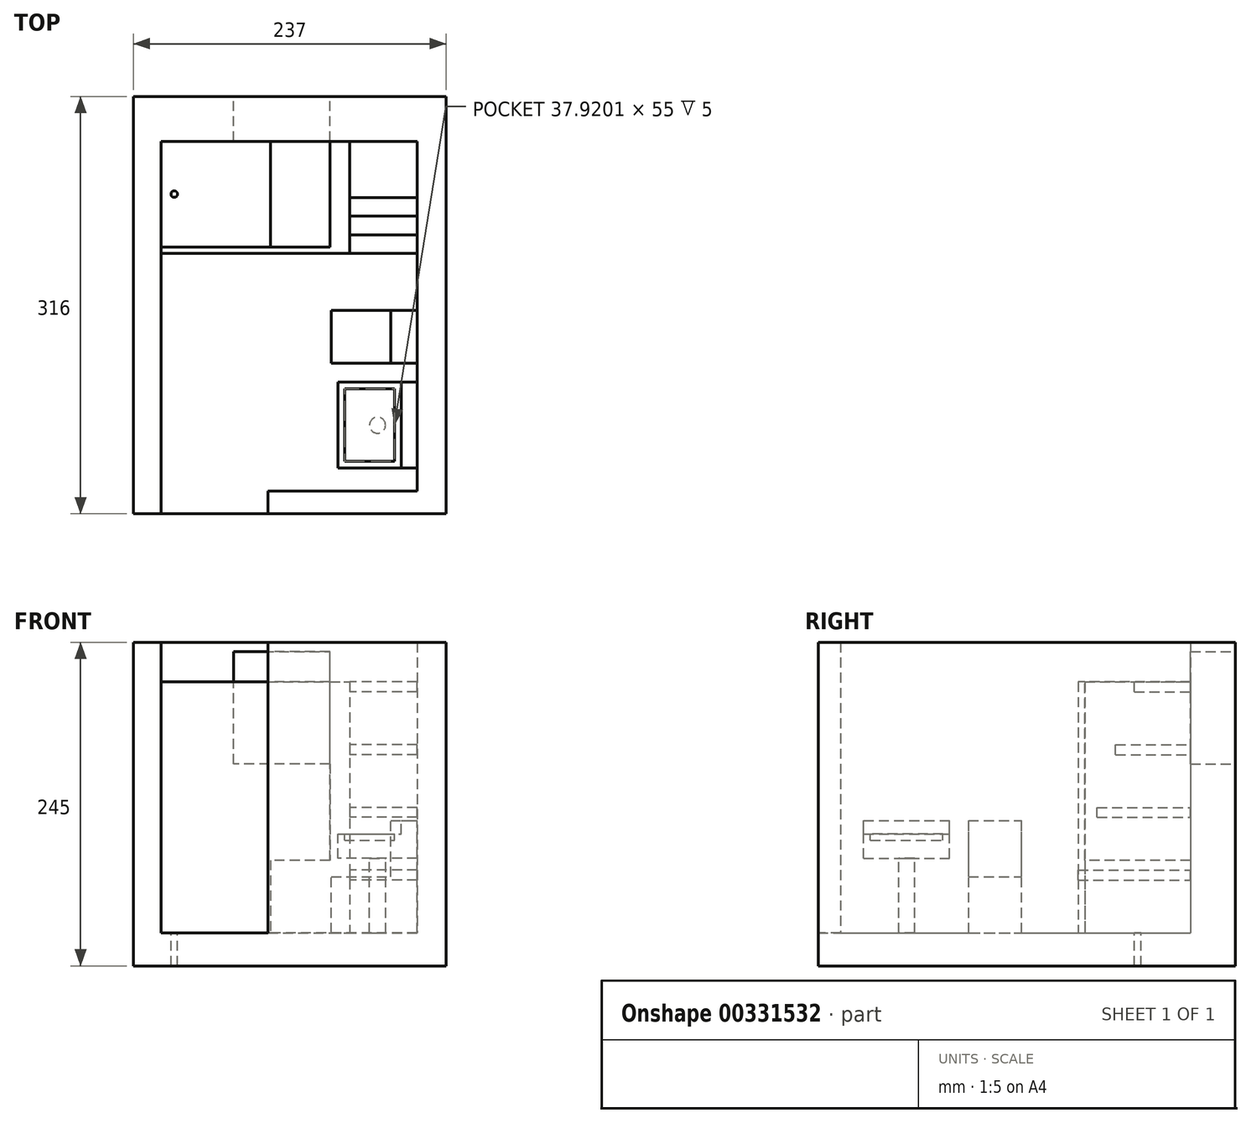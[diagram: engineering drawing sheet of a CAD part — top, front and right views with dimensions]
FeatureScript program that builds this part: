
annotation { "Feature Type Name" : "Feature", "Feature Type Description" : "" }
export const myFeature = defineFeature(function(context is Context, id is Id, definition is map)
    precondition{}
    {
        {
            var Q0;
            Q0=qCreatedBy(makeId("Top.planeOp"),FACE);
            var sketch = newSketch(context, id + "F0", { "sketchPlane" : qUnion([Q0])});
            skLineSegment(sketch, "E0", {"start": v(1313, 440) * mm, "end": v(1313, 406) * mm});
            skLineSegment(sketch, "E1", {"start": v(1313, -267) * mm, "end": v(1313, -301) * mm});
            skLineSegment(sketch, "E2", {"start": v(1313, -301) * mm, "end": v(647, -301) * mm});
            skLineSegment(sketch, "E3", {"start": v(1279, -267) * mm, "end": v(647, -267) * mm});
            skLineSegment(sketch, "E4", {"start": v(1279, 406) * mm, "end": v(688, 406) * mm});
            skLineSegment(sketch, "E5", {"start": v(688, 406) * mm, "end": v(688, -75) * mm});
            skLineSegment(sketch, "E6", {"start": v(688, -75) * mm, "end": v(413, -75) * mm});
            skLineSegment(sketch, "E7", {"start": v(647, -301) * mm, "end": v(647, -267) * mm});
            skLineSegment(sketch, "E8", {"start": v(536, -301) * mm, "end": v(536, -267) * mm});
            skLineSegment(sketch, "E9", {"start": v(536, -267) * mm, "end": v(328, -267) * mm});
            skLineSegment(sketch, "E10", {"start": v(328, -267) * mm, "end": v(328, -407) * mm});
            skLineSegment(sketch, "E11", {"start": v(328, -407) * mm, "end": v(-40, -407) * mm});
            skLineSegment(sketch, "E12", {"start": v(-40, -407) * mm, "end": v(-40, -188) * mm});
            skLineSegment(sketch, "E13", {"start": v(-40, -188) * mm, "end": v(-105, -188) * mm});
            skLineSegment(sketch, "E14", {"start": v(536, -301) * mm, "end": v(362, -301) * mm});
            skLineSegment(sketch, "E15", {"start": v(362, -301) * mm, "end": v(362, -440) * mm});
            skLineSegment(sketch, "E16", {"start": v(-60, -407) * mm, "end": v(-60, -215) * mm});
            skLineSegment(sketch, "E17", {"start": v(-60, -215) * mm, "end": v(-105, -215) * mm});
            skLineSegment(sketch, "E18", {"start": v(-105, -188) * mm, "end": v(-105, -215) * mm});
            skLineSegment(sketch, "E19", {"start": v(-60, -407) * mm, "end": v(-282, -407) * mm});
            skLineSegment(sketch, "E20", {"start": v(-282, -407) * mm, "end": v(-282, -287) * mm});
            skLineSegment(sketch, "E21", {"start": v(-282, -287) * mm, "end": v(-330, -287) * mm});
            skLineSegment(sketch, "E22", {"start": v(-330, -287) * mm, "end": v(-330, -407) * mm});
            skLineSegment(sketch, "E23", {"start": v(-330, -407) * mm, "end": v(-497, -407) * mm});
            skLineSegment(sketch, "E24", {"start": v(-197, -188) * mm, "end": v(-197, -215) * mm});
            skLineSegment(sketch, "E25", {"start": v(-197, -188) * mm, "end": v(-765, -188) * mm});
            skLineSegment(sketch, "E26", {"start": v(-197, -215) * mm, "end": v(-497, -215) * mm});
            skLineSegment(sketch, "E27", {"start": v(-497, -215) * mm, "end": v(-497, -231) * mm});
            skLineSegment(sketch, "E28", {"start": v(-497, -231) * mm, "end": v(-497, -293) * mm});
            skLineSegment(sketch, "E29", {"start": v(-497, -407) * mm, "end": v(-497, -349) * mm});
            skLineSegment(sketch, "E30", {"start": v(413, -75) * mm, "end": v(413, -54) * mm});
            skLineSegment(sketch, "E31", {"start": v(413, -54) * mm, "end": v(667, -54) * mm});
            skLineSegment(sketch, "E32", {"start": v(667, -54) * mm, "end": v(667, 406) * mm});
            skLineSegment(sketch, "E33", {"start": v(667, 406) * mm, "end": v(495, 406) * mm});
            skLineSegment(sketch, "E34", {"start": v(312, 406) * mm, "end": v(391, 406) * mm});
            skLineSegment(sketch, "E35", {"start": v(391, 406) * mm, "end": v(391, 440) * mm});
            skLineSegment(sketch, "E36", {"start": v(495, 406) * mm, "end": v(495, 440) * mm});
            skLineSegment(sketch, "E37", {"start": v(1313, 440) * mm, "end": v(495, 440) * mm});
            skLineSegment(sketch, "E38", {"start": v(312, -75) * mm, "end": v(60, -75) * mm});
            skLineSegment(sketch, "E39", {"start": v(-1279, 406) * mm, "end": v(-1279, 7) * mm});
            skLineSegment(sketch, "E40", {"start": v(-790, 406) * mm, "end": v(-790, 7) * mm});
            skLineSegment(sketch, "E41", {"start": v(-1279, 7) * mm, "end": v(-910, 7) * mm});
            skLineSegment(sketch, "E42", {"start": v(-790, 7) * mm, "end": v(-808, 7) * mm});
            skLineSegment(sketch, "E43", {"start": v(-765, -188) * mm, "end": v(-765, -208) * mm});
            skLineSegment(sketch, "E44", {"start": v(290, 141) * mm, "end": v(290, 406) * mm});
            skLineSegment(sketch, "E45", {"start": v(290, 141) * mm, "end": v(75, 141) * mm});
            skLineSegment(sketch, "E46", {"start": v(75, -46) * mm, "end": v(75, 141) * mm});
            skLineSegment(sketch, "E47", {"start": v(60, -75) * mm, "end": v(60, -46) * mm});
            skLineSegment(sketch, "E48", {"start": v(391, 406) * mm, "end": v(312, 406) * mm});
            skLineSegment(sketch, "E49", {"start": v(-139, 406) * mm, "end": v(-139, 440) * mm});
            skLineSegment(sketch, "E50", {"start": v(-318, 406) * mm, "end": v(-318, 440) * mm});
            skLineSegment(sketch, "E51", {"start": v(-515, 406) * mm, "end": v(-515, 440) * mm});
            skLineSegment(sketch, "E52", {"start": v(-694, 406) * mm, "end": v(-694, 440) * mm});
            skLineSegment(sketch, "E53", {"start": v(-770, 406) * mm, "end": v(-770, 9) * mm});
            skLineSegment(sketch, "E54", {"start": v(-694, 406) * mm, "end": v(-770, 406) * mm});
            skLineSegment(sketch, "E55", {"start": v(75, 406) * mm, "end": v(-139, 406) * mm});
            skLineSegment(sketch, "E56", {"start": v(-318, 406) * mm, "end": v(-515, 406) * mm});
            skLineSegment(sketch, "E57", {"start": v(-318, 440) * mm, "end": v(-515, 440) * mm});
            skLineSegment(sketch, "E58", {"start": v(-770, 9) * mm, "end": v(-754, 9) * mm});
            skLineSegment(sketch, "E59", {"start": v(-677, 9) * mm, "end": v(-659, 9) * mm});
            skLineSegment(sketch, "E60", {"start": v(-659, 9) * mm, "end": v(-659, -5) * mm});
            skLineSegment(sketch, "E61", {"start": v(-659, -5) * mm, "end": v(-659, -46) * mm});
            skLineSegment(sketch, "E62", {"start": v(-659, -46) * mm, "end": v(-60, -46) * mm});
            skLineSegment(sketch, "E63", {"start": v(-60, -75) * mm, "end": v(-60, -46) * mm});
            skLineSegment(sketch, "E64", {"start": v(60, -75) * mm, "end": v(128, -75) * mm});
            skLineSegment(sketch, "E65", {"start": v(60, -46) * mm, "end": v(75, -46) * mm});
            skLineSegment(sketch, "E66", {"start": v(96, -46) * mm, "end": v(290, -46) * mm});
            skLineSegment(sketch, "E67", {"start": v(-60, -75) * mm, "end": v(-677, -75) * mm});
            skLineSegment(sketch, "E68", {"start": v(-677, 9) * mm, "end": v(-677, -75) * mm});
            skLineSegment(sketch, "E69", {"start": v(-754, 9) * mm, "end": v(-754, -13) * mm});
            skLineSegment(sketch, "E70", {"start": v(-808, 7) * mm, "end": v(-808, -13) * mm});
            skLineSegment(sketch, "E71", {"start": v(-808, -13) * mm, "end": v(-754, -13) * mm});
            skLineSegment(sketch, "E72", {"start": v(-910, 7) * mm, "end": v(-910, -29) * mm});
            skLineSegment(sketch, "E73", {"start": v(-1279, -406) * mm, "end": v(-935, -406) * mm});
            skLineSegment(sketch, "E74", {"start": v(-1313, -440) * mm, "end": v(-935, -440) * mm});
            skLineSegment(sketch, "E75", {"start": v(-910, -29) * mm, "end": v(-935, -29) * mm});
            skLineSegment(sketch, "E76", {"start": v(-935, -13) * mm, "end": v(-1279, -13) * mm});
            skLineSegment(sketch, "E77", {"start": v(-910, -132) * mm, "end": v(-935, -132) * mm});
            skLineSegment(sketch, "E78", {"start": v(-910, -29) * mm, "end": v(-910, -13) * mm});
            skLineSegment(sketch, "E79", {"start": v(-935, -406) * mm, "end": v(-935, -132) * mm});
            skLineSegment(sketch, "E80", {"start": v(-935, -29) * mm, "end": v(-935, -13) * mm});
            skLineSegment(sketch, "E81", {"start": v(-877, -208) * mm, "end": v(-877, -188) * mm});
            skLineSegment(sketch, "E82", {"start": v(-910, -132) * mm, "end": v(-910, -188) * mm});
            skLineSegment(sketch, "E83", {"start": v(-877, -188) * mm, "end": v(-910, -188) * mm});
            skLineSegment(sketch, "E84", {"start": v(-877, -208) * mm, "end": v(-904, -208) * mm});
            skLineSegment(sketch, "E85", {"start": v(-904, -208) * mm, "end": v(-904, -406) * mm});
            skLineSegment(sketch, "E86", {"start": v(-904, -406) * mm, "end": v(-648, -406) * mm});
            skLineSegment(sketch, "E87", {"start": v(-765, -208) * mm, "end": v(-648, -208) * mm});
            skLineSegment(sketch, "E88", {"start": v(-648, -208) * mm, "end": v(-648, -273) * mm});
            skLineSegment(sketch, "E89", {"start": v(-648, -406) * mm, "end": v(-648, -343) * mm});
            skLineSegment(sketch, "E90", {"start": v(-935, -440) * mm, "end": v(362, -440) * mm});
            skLineSegment(sketch, "E91", {"start": v(151, 406) * mm, "end": v(151, 440) * mm});
            skLineSegment(sketch, "E92", {"start": v(224, 406) * mm, "end": v(224, 440) * mm});
            skLineSegment(sketch, "E93", {"start": v(290, 406) * mm, "end": v(224, 406) * mm});
            skLineSegment(sketch, "E94", {"start": v(151, 406) * mm, "end": v(96, 406) * mm});
            skLineSegment(sketch, "E95", {"start": v(391, 440) * mm, "end": v(224, 440) * mm});
            skLineSegment(sketch, "E96", {"start": v(151, 440) * mm, "end": v(-139, 440) * mm});
            skLineSegment(sketch, "E97", {"start": v(-907, 406) * mm, "end": v(-907, 440) * mm});
            skLineSegment(sketch, "E98", {"start": v(-1085, 406) * mm, "end": v(-1085, 440) * mm});
            skLineSegment(sketch, "E99", {"start": v(-790, 406) * mm, "end": v(-907, 406) * mm});
            skLineSegment(sketch, "E100", {"start": v(-1085, 406) * mm, "end": v(-1279, 406) * mm});
            skLineSegment(sketch, "E101", {"start": v(-694, 440) * mm, "end": v(-907, 440) * mm});
            skLineSegment(sketch, "E102", {"start": v(-1085, 440) * mm, "end": v(-1313, 440) * mm});
            skLineSegment(sketch, "E103", {"start": v(-1279, -118) * mm, "end": v(-1313, -118) * mm});
            skLineSegment(sketch, "E104", {"start": v(-1279, -297) * mm, "end": v(-1313, -297) * mm});
            skLineSegment(sketch, "E105", {"start": v(-1279, -13) * mm, "end": v(-1279, -118) * mm});
            skLineSegment(sketch, "E106", {"start": v(-1279, -297) * mm, "end": v(-1279, -406) * mm});
            skLineSegment(sketch, "E107", {"start": v(-1313, 440) * mm, "end": v(-1313, -118) * mm});
            skLineSegment(sketch, "E108", {"start": v(-1313, -297) * mm, "end": v(-1313, -440) * mm});
            skLineSegment(sketch, "E109", {"start": v(-648, -273) * mm, "end": v(-630, -273) * mm});
            skLineSegment(sketch, "E110", {"start": v(-648, -343) * mm, "end": v(-630, -343) * mm});
            skLineSegment(sketch, "E111", {"start": v(-515, -349) * mm, "end": v(-497, -349) * mm});
            skLineSegment(sketch, "E112", {"start": v(-515, -293) * mm, "end": v(-497, -293) * mm});
            skLineSegment(sketch, "E113", {"start": v(-515, -349) * mm, "end": v(-515, -406) * mm});
            skLineSegment(sketch, "E114", {"start": v(-630, -343) * mm, "end": v(-630, -406) * mm});
            skLineSegment(sketch, "E115", {"start": v(-630, -406) * mm, "end": v(-515, -406) * mm});
            skLineSegment(sketch, "E116", {"start": v(-630, -273) * mm, "end": v(-630, -206) * mm});
            skLineSegment(sketch, "E117", {"start": v(-630, -206) * mm, "end": v(-515, -206) * mm});
            skLineSegment(sketch, "E118", {"start": v(-515, -293) * mm, "end": v(-515, -206) * mm});
            skLineSegment(sketch, "E119", {"start": v(290, 43) * mm, "end": v(312, 43) * mm});
            skLineSegment(sketch, "E120", {"start": v(290, 124) * mm, "end": v(312, 124) * mm});
            skLineSegment(sketch, "E121", {"start": v(312, -75) * mm, "end": v(312, 43) * mm});
            skLineSegment(sketch, "E122", {"start": v(312, 124) * mm, "end": v(312, 406) * mm});
            skLineSegment(sketch, "E123", {"start": v(290, -46) * mm, "end": v(290, 43) * mm});
            skLineSegment(sketch, "E124", {"start": v(96, 222) * mm, "end": v(75, 222) * mm});
            skLineSegment(sketch, "E125", {"start": v(96, 222) * mm, "end": v(96, 406) * mm});
            skLineSegment(sketch, "E126", {"start": v(75, 222) * mm, "end": v(75, 406) * mm});
            skLineSegment(sketch, "E127", {"start": v(96, -46) * mm, "end": v(96, 124) * mm});
            skLineSegment(sketch, "E128", {"start": v(290, 124) * mm, "end": v(96, 124) * mm});
            skLineSegment(sketch, "E129", {"start": v(1279, -219) * mm, "end": v(1313, -219) * mm});
            skLineSegment(sketch, "E130", {"start": v(1279, -26) * mm, "end": v(1313, -26) * mm});
            skLineSegment(sketch, "E131", {"start": v(1279, 46) * mm, "end": v(1313, 46) * mm});
            skLineSegment(sketch, "E132", {"start": v(1279, 239) * mm, "end": v(1313, 239) * mm});
            skLineSegment(sketch, "E133", {"start": v(1313, 406) * mm, "end": v(1313, 239) * mm});
            skLineSegment(sketch, "E134", {"start": v(1279, 406) * mm, "end": v(1279, 239) * mm});
            skLineSegment(sketch, "E135", {"start": v(1313, 46) * mm, "end": v(1313, -26) * mm});
            skLineSegment(sketch, "E136", {"start": v(1313, -219) * mm, "end": v(1313, -267) * mm});
            skLineSegment(sketch, "E137", {"start": v(1279, 46) * mm, "end": v(1279, -26) * mm});
            skLineSegment(sketch, "E138", {"start": v(1279, -219) * mm, "end": v(1279, -267) * mm});
            skLineSegment(sketch, "E139", {"start": v(1313, -301) * mm, "end": v(1313, 440) * mm});
            skLineSegment(sketch, "E140", {"start": v(1313, -301) * mm, "end": v(362, -301) * mm});
            skLineSegment(sketch, "E141", {"start": v(362, -440) * mm, "end": v(-1313, -440) * mm});
            skLineSegment(sketch, "E142", {"start": v(-1313, 440) * mm, "end": v(-1313, -440) * mm});
            skLineSegment(sketch, "E143", {"start": v(-1313, 440) * mm, "end": v(1313, 440) * mm});
            skSolve(sketch);
        }
        {
            var Q0;
            Q0=qCreatedBy(makeId("Top.planeOp"),FACE);
            var sketch = newSketch(context, id + "F1", { "sketchPlane" : qUnion([Q0])});
            skLineSegment(sketch, "E144.0", {"start": v(290, 406) * mm, "end": v(224, 406) * mm});
            skLineSegment(sketch, "E145.0", {"start": v(75, 440) * mm, "end": v(312, 440) * mm});
            skLineSegment(sketch, "E146.0", {"start": v(151, 406) * mm, "end": v(96, 406) * mm});
            skLineSegment(sketch, "E147.0", {"start": v(96, 222) * mm, "end": v(96, 406) * mm});
            skLineSegment(sketch, "E148.0", {"start": v(312, 124) * mm, "end": v(312, 406) * mm});
            skLineSegment(sketch, "E149.0", {"start": v(290, 141) * mm, "end": v(290, 406) * mm});
            skLineSegment(sketch, "E150.0", {"start": v(75, 124) * mm, "end": v(75, 141) * mm});
            skLineSegment(sketch, "E151", {"start": v(312, 406) * mm, "end": v(312, 440) * mm});
            skLineSegment(sketch, "E152", {"start": v(75, 406) * mm, "end": v(75, 440) * mm});
            skLineSegment(sketch, "E153", {"start": v(151, 406) * mm, "end": v(224, 406) * mm});
            skLineSegment(sketch, "E154", {"start": v(290, 124) * mm, "end": v(312, 124) * mm});
            skLineSegment(sketch, "E155", {"start": v(96, 124) * mm, "end": v(75, 124) * mm});
            skPoint(sketch, "E156.orphan", {"position": v(1313, 440) * mm});
            skPoint(sketch, "E157.orphan", {"position": v(75, -46) * mm});
            skPoint(sketch, "E158.orphan", {"position": v(-1313, 440) * mm});
            skPoint(sketch, "E159.end.orphan", {"position": v(96, 141) * mm});
            skPoint(sketch, "E160.orphan", {"position": v(290, 141) * mm});
            skLineSegment(sketch, "E161", {"start": v(290, 141) * mm, "end": v(177, 141) * mm});
            skLineSegment(sketch, "E162", {"start": v(290, 124) * mm, "end": v(177, 124) * mm});
            skPoint(sketch, "E163.end.orphan", {"position": v(75, 141) * mm});
            skPoint(sketch, "E164.0.start.orphan", {"position": v(75, 222) * mm});
            skLineSegment(sketch, "E165", {"start": v(75, 406) * mm, "end": v(75, 141) * mm});
            skLineSegment(sketch, "E166", {"start": v(96, 124) * mm, "end": v(96, 222) * mm});
            skLineSegment(sketch, "E167", {"start": v(177, 141) * mm, "end": v(177, 124) * mm});
            skSolve(sketch);
        }
        {
            var Q0;
            Q0 = qSketchRegion(id + "F1", true);
            extrude(context, id + "F2", {"entities" : qUnion([Q0]), "depth" : 220 * mm});
        }
        {
            var Q0;
            Q0=makeQuery(id+"F2.opExtrude","CAP_FACE",FACE,{"disambiguationData":[OSD([sQuery(id+"F1.wireOp",EDGE,"E144.0"),sQuery(id+"F1.wireOp",EDGE,"E145.0"),sQuery(id+"F1.wireOp",EDGE,"E146.0"),sQuery(id+"F1.wireOp",EDGE,"E147.0"),sQuery(id+"F1.wireOp",EDGE,"E148.0"),sQuery(id+"F1.wireOp",EDGE,"E149.0"),sQuery(id+"F1.wireOp",EDGE,"E150.0"),sQuery(id+"F1.wireOp",EDGE,"E151"),sQuery(id+"F1.wireOp",EDGE,"E152"),sQuery(id+"F1.wireOp",EDGE,"E153"),sQuery(id+"F1.wireOp",EDGE,"E154"),sQuery(id+"F1.wireOp",EDGE,"E155"),sQuery(id+"F1.wireOp",EDGE,"E161"),sQuery(id+"F1.wireOp",EDGE,"E162"),sQuery(id+"F1.wireOp",EDGE,"E165"),sQuery(id+"F1.wireOp",EDGE,"E166"),sQuery(id+"F1.wireOp",EDGE,"E167")])],"isStart":false});
            var sketch = newSketch(context, id + "F3", { "sketchPlane" : qUnion([Q0])});
            skLineSegment(sketch, "E168", {"start": v(151, 406) * mm, "end": v(151, 440) * mm});
            skLineSegment(sketch, "E169", {"start": v(224, 406) * mm, "end": v(224, 440) * mm});
            skLineSegment(sketch, "E170.0", {"start": v(151, 406) * mm, "end": v(224, 406) * mm});
            skLineSegment(sketch, "E171", {"start": v(224, 440) * mm, "end": v(151, 440) * mm});
            skPoint(sketch, "E172.0.start.orphan", {"position": v(290, 406) * mm});
            skPoint(sketch, "E173.0.end.orphan", {"position": v(96, 406) * mm});
            skSolve(sketch);
        }
        {
            var Q0;
            Q0 = qSketchRegion(id + "F3", true);
            extrude(context, id + "F4", {"entities" : qUnion([Q0]), "operationType" : NewBodyOperationType.REMOVE, "oppositeDirection" : true, "depth" : 92 * mm});
        }
        {
            var Q0;
            {var subQ0=sQuery(id+"F1.wireOp",EDGE,"E166");var subQ1=sQuery(id+"F1.wireOp",EDGE,"E147.0");var subQ2=sQuery(id+"F1.wireOp",EDGE,"E145.0");var subQ3=sQuery(id+"F1.wireOp",EDGE,"E165");var subQ4=sQuery(id+"F1.wireOp",EDGE,"E152");var subQ5=sQuery(id+"F1.wireOp",EDGE,"E150.0");var subQ6=sQuery(id+"F1.wireOp",EDGE,"E153");var subQ7=sQuery(id+"F1.wireOp",EDGE,"E146.0");var subQ8=sQuery(id+"F1.wireOp",EDGE,"E144.0");var subQ9=sQuery(id+"F1.wireOp",EDGE,"E155");Q0=makeQuery(id+"F4.boolean.opBoolean","SPLIT",FACE,{"disambiguationData":[TD([makeQuery(id+"F2.opExtrude","SWEPT_FACE",FACE,{"disambiguationData":[OSD([subQ9])]})])],"derivedFrom":makeQuery(id+"F2.opExtrude","CAP_FACE",FACE,{"disambiguationData":[OSD([subQ8,subQ2,subQ7,subQ1,sQuery(id+"F1.wireOp",EDGE,"E148.0"),sQuery(id+"F1.wireOp",EDGE,"E149.0"),subQ5,sQuery(id+"F1.wireOp",EDGE,"E151"),subQ4,subQ6,sQuery(id+"F1.wireOp",EDGE,"E154"),subQ9,sQuery(id+"F1.wireOp",EDGE,"E161"),sQuery(id+"F1.wireOp",EDGE,"E162"),subQ3,subQ0,sQuery(id+"F1.wireOp",EDGE,"E167")])],"isStart":false})});}
            var sketch = newSketch(context, id + "F5", { "sketchPlane" : qUnion([Q0])});
            skLineSegment(sketch, "E174.0", {"start": v(151, 440) * mm, "end": v(224, 440) * mm});
            skLineSegment(sketch, "E175.0", {"start": v(224, 406) * mm, "end": v(151, 406) * mm});
            skPoint(sketch, "E176.0", {"position": v(224, 423) * mm});
            skPoint(sketch, "E177.0", {"position": v(151, 423) * mm});
            skLineSegment(sketch, "E178.0", {"start": v(151, 406) * mm, "end": v(151, 440) * mm});
            skLineSegment(sketch, "E179.0", {"start": v(224, 406) * mm, "end": v(224, 440) * mm});
            skSolve(sketch);
        }
        {
            var Q0;
            Q0 = qSketchRegion(id + "F5", true);
            extrude(context, id + "F6", {"entities" : qUnion([Q0]), "operationType" : NewBodyOperationType.ADD, "oppositeDirection" : true, "depth" : 7 * mm});
        }
        {
            var Q0;
            Q0=makeQuery(id+"F2.opExtrude","CAP_FACE",FACE,{"disambiguationData":[OSD([sQuery(id+"F1.wireOp",EDGE,"E144.0"),sQuery(id+"F1.wireOp",EDGE,"E145.0"),sQuery(id+"F1.wireOp",EDGE,"E146.0"),sQuery(id+"F1.wireOp",EDGE,"E147.0"),sQuery(id+"F1.wireOp",EDGE,"E148.0"),sQuery(id+"F1.wireOp",EDGE,"E149.0"),sQuery(id+"F1.wireOp",EDGE,"E150.0"),sQuery(id+"F1.wireOp",EDGE,"E151"),sQuery(id+"F1.wireOp",EDGE,"E152"),sQuery(id+"F1.wireOp",EDGE,"E153"),sQuery(id+"F1.wireOp",EDGE,"E154"),sQuery(id+"F1.wireOp",EDGE,"E155"),sQuery(id+"F1.wireOp",EDGE,"E161"),sQuery(id+"F1.wireOp",EDGE,"E162"),sQuery(id+"F1.wireOp",EDGE,"E165"),sQuery(id+"F1.wireOp",EDGE,"E166"),sQuery(id+"F1.wireOp",EDGE,"E167")])],"isStart":true});
            var sketch = newSketch(context, id + "F7", { "sketchPlane" : qUnion([Q0])});
            skLineSegment(sketch, "E180.bottom", {"start": v(312, -440) * mm, "end": v(75, -440) * mm});
            skLineSegment(sketch, "E180.top", {"start": v(312, -124) * mm, "end": v(75, -124) * mm});
            skLineSegment(sketch, "E180.left", {"start": v(312, -440) * mm, "end": v(312, -124) * mm});
            skLineSegment(sketch, "E180.right", {"start": v(75, -440) * mm, "end": v(75, -124) * mm});
            skSolve(sketch);
        }
        {
            var Q0;
            Q0 = qSketchRegion(id + "F7", true);
            extrude(context, id + "F8", {"entities" : qUnion([Q0]), "operationType" : NewBodyOperationType.ADD, "depth" : 25 * mm});
        }
        {
            var Q0;
            Q0=makeQuery(id+"F2.opExtrude","SWEPT_FACE",FACE,{"disambiguationData":[OSD([sQuery(id+"F1.wireOp",EDGE,"E149.0")])]});
            var sketch = newSketch(context, id + "F9", { "sketchPlane" : qUnion([Q0])});
            skLineSegment(sketch, "E181", {"start": v(-191, 42.5) * mm, "end": v(-258, 42.5) * mm, "construction": true});
            skLineSegment(sketch, "E182.bottom", {"start": v(-238, 0) * mm, "end": v(-278, 0) * mm});
            skLineSegment(sketch, "E182.top", {"start": v(-238, 85) * mm, "end": v(-278, 85) * mm});
            skLineSegment(sketch, "E182.left", {"start": v(-238, 0) * mm, "end": v(-238, 85) * mm});
            skLineSegment(sketch, "E182.right", {"start": v(-278, 0) * mm, "end": v(-278, 85) * mm});
            skPoint(sketch, "E182.middle", {"position": v(-258, 42.5) * mm});
            skSolve(sketch);
        }
        {
            var Q0;
            Q0 = qSketchRegion(id + "F9", true);
            extrude(context, id + "F10", {"entities" : qUnion([Q0]), "depth" : 10 * mm});
        }
        {
            var Q0;
            Q0=makeQuery(id+"F8.opExtrude","CAP_FACE",FACE,{"disambiguationData":[OSD([sQuery(id+"F7.wireOp",EDGE,"E180.bottom"),sQuery(id+"F7.wireOp",EDGE,"E180.top"),sQuery(id+"F7.wireOp",EDGE,"E180.left"),sQuery(id+"F7.wireOp",EDGE,"E180.right")])],"isStart":true});
            var sketch = newSketch(context, id + "F11", { "sketchPlane" : qUnion([Q0])});
            skCircle(sketch, "E183", {"center": v(106, 366) * mm, "radius": 2.5 * mm});
            skSolve(sketch);
        }
        {
            var Q0;
            Q0 = qSketchRegion(id + "F11", true);
            extrude(context, id + "F12", {"entities" : qUnion([Q0]), "operationType" : NewBodyOperationType.REMOVE, "oppositeDirection" : true, "depth" : 25 * mm});
        }
        {
            var Q0;
            Q0 = qSketchRegion(id + "F9", true);
            extrude(context, id + "F13", {"entities" : qUnion([Q0]), "operationType" : NewBodyOperationType.ADD, "depth" : 20 * mm});
        }
        {
            var Q0;
            Q0=makeQuery(id+"F13.opExtrude","CAP_FACE",FACE,{"disambiguationData":[OSD([sQuery(id+"F9.wireOp",EDGE,"E182.bottom"),sQuery(id+"F9.wireOp",EDGE,"E182.top"),sQuery(id+"F9.wireOp",EDGE,"E182.left"),sQuery(id+"F9.wireOp",EDGE,"E182.right")])],"isStart":false});
            var sketch = newSketch(context, id + "F14", { "sketchPlane" : qUnion([Q0])});
            skLineSegment(sketch, "E184.0", {"start": v(-238, 42.5) * mm, "end": v(-258, 42.5) * mm});
            skLineSegment(sketch, "E185.0", {"start": v(-238, 0) * mm, "end": v(-238, 42.5) * mm});
            skLineSegment(sketch, "E186.0", {"start": v(-278, 0) * mm, "end": v(-278, 42.5) * mm});
            skLineSegment(sketch, "E187.0", {"start": v(-238, 0) * mm, "end": v(-278, 0) * mm});
            skLineSegment(sketch, "E188", {"start": v(-258, 42.5) * mm, "end": v(-278, 42.5) * mm});
            skPoint(sketch, "E189.orphan", {"position": v(-278, 85) * mm});
            skPoint(sketch, "E190.orphan", {"position": v(-238, 85) * mm});
            skPoint(sketch, "E191.orphan", {"position": v(-191, 42.5) * mm});
            skSolve(sketch);
        }
        {
            var Q0;
            Q0 = qSketchRegion(id + "F14", true);
            extrude(context, id + "F15", {"entities" : qUnion([Q0]), "operationType" : NewBodyOperationType.ADD, "depth" : 45 * mm});
        }
        {
            var Q0;
            Q0=makeQuery(id+"F9.imprint","IMPRINT",FACE,{"disambiguationData":[TD([[makeQuery(id+"F9.imprint","IMPRINT",EDGE,{"derivedFrom":sQuery(id+"F9.wireOp",EDGE,"E182.top")}),-1.0]])]});
            var sketch = newSketch(context, id + "F16", { "sketchPlane" : qUnion([Q0])});
            skLineSegment(sketch, "E192.0", {"start": v(-191, 42.5) * mm, "end": v(-258, 42.5) * mm, "construction": true});
            skPoint(sketch, "E193.0", {"position": v(-258, 0) * mm});
            skLineSegment(sketch, "E194", {"start": v(-191, 199.1) * mm, "end": v(-191, 0) * mm, "construction": true});
            skLineSegment(sketch, "E195.bottom", {"start": v(-158.5, 0) * mm, "end": v(-223.5, 0) * mm});
            skLineSegment(sketch, "E195.top", {"start": v(-158.5, 85) * mm, "end": v(-223.5, 85) * mm});
            skLineSegment(sketch, "E195.left", {"start": v(-158.5, 0) * mm, "end": v(-158.5, 85) * mm});
            skLineSegment(sketch, "E195.right", {"start": v(-223.5, 0) * mm, "end": v(-223.5, 85) * mm});
            skPoint(sketch, "E195.middle", {"position": v(-191, 42.5) * mm});
            skSolve(sketch);
        }
        {
            var Q0;
            Q0 = qSketchRegion(id + "F16", true);
            extrude(context, id + "F17", {"entities" : qUnion([Q0]), "depth" : 60 * mm});
        }
        {
            var Q0;
            Q0=makeQuery(id+"F17.opExtrude","SWEPT_FACE",FACE,{"disambiguationData":[OSD([sQuery(id+"F16.wireOp",EDGE,"E195.top")])]});
            var sketch = newSketch(context, id + "F18", { "sketchPlane" : qUnion([Q0])});
            skLineSegment(sketch, "E196.bottom", {"start": v(277.92, 223.5) * mm, "end": v(230, 223.5) * mm});
            skLineSegment(sketch, "E196.top", {"start": v(277.92, 158.5) * mm, "end": v(230, 158.5) * mm});
            skLineSegment(sketch, "E196.left", {"start": v(277.92, 223.5) * mm, "end": v(277.92, 158.5) * mm});
            skLineSegment(sketch, "E196.right", {"start": v(230, 223.5) * mm, "end": v(230, 158.5) * mm});
            skSolve(sketch);
        }
        {
            var Q0;
            Q0 = qSketchRegion(id + "F18", true);
            extrude(context, id + "F19", {"entities" : qUnion([Q0]), "operationType" : NewBodyOperationType.REMOVE, "oppositeDirection" : true, "depth" : 10 * mm});
        }
        {
            var Q0;
            Q0=makeQuery(id+"F17.opExtrude","CAP_FACE",FACE,{"disambiguationData":[OSD([sQuery(id+"F16.wireOp",EDGE,"E195.bottom"),sQuery(id+"F16.wireOp",EDGE,"E195.top"),sQuery(id+"F16.wireOp",EDGE,"E195.left"),sQuery(id+"F16.wireOp",EDGE,"E195.right")])],"isStart":false});
            var sketch = newSketch(context, id + "F20", { "sketchPlane" : qUnion([Q0])});
            skLineSegment(sketch, "E197.bottom", {"start": v(-223.5, 0) * mm, "end": v(-158.5, 0) * mm});
            skLineSegment(sketch, "E197.top", {"start": v(-223.5, 56.5) * mm, "end": v(-158.5, 56.5) * mm});
            skLineSegment(sketch, "E197.left", {"start": v(-223.5, 0) * mm, "end": v(-223.5, 56.5) * mm});
            skLineSegment(sketch, "E197.right", {"start": v(-158.5, 0) * mm, "end": v(-158.5, 56.5) * mm});
            skSolve(sketch);
        }
        {
            var Q0;
            Q0 = qSketchRegion(id + "F20", true);
            var Q1;
            Q1=makeQuery(id+"F2.opExtrude","SWEPT_FACE",FACE,{"disambiguationData":[OSD([sQuery(id+"F1.wireOp",EDGE,"E149.0")])]});
            extrude(context, id + "F21", {"entities" : qUnion([Q0]), "operationType" : NewBodyOperationType.REMOVE, "endBound" : BoundingType.UP_TO_SURFACE, "oppositeDirection" : true, "endBoundEntityFace" : qUnion([Q1]), "depth" : 25 * mm});
        }
        {
            var Q0;
            Q0=makeQuery(id+"F21.boolean.opBoolean","COPY",FACE,{"derivedFrom":makeQuery(id+"F21.opExtrude","SWEPT_FACE",FACE,{"disambiguationData":[OSD([sQuery(id+"F20.wireOp",EDGE,"E197.top")])]})});
            var sketch = newSketch(context, id + "F22", { "sketchPlane" : qUnion([Q0])});
            skCircle(sketch, "E198", {"center": v(260, -191) * mm, "radius": 6.07 * mm});
            skPoint(sketch, "E198.centerSnap0", {"position": v(230, -191) * mm});
            skPoint(sketch, "E198.centerSnap1", {"position": v(260, -223.5) * mm});
            skSolve(sketch);
        }
        {
            var Q0;
            Q0 = qSketchRegion(id + "F22", true);
            var Q1;
            Q1=makeQuery(id+"F8.opExtrude","CAP_FACE",FACE,{"disambiguationData":[OSD([sQuery(id+"F7.wireOp",EDGE,"E180.bottom"),sQuery(id+"F7.wireOp",EDGE,"E180.top"),sQuery(id+"F7.wireOp",EDGE,"E180.left"),sQuery(id+"F7.wireOp",EDGE,"E180.right")])],"isStart":true});
            extrude(context, id + "F23", {"entities" : qUnion([Q0]), "operationType" : NewBodyOperationType.ADD, "endBound" : BoundingType.UP_TO_SURFACE, "endBoundEntityFace" : qUnion([Q1]), "depth" : 25 * mm});
        }
        {
            var Q0;
            Q0=makeQuery(id+"F19.boolean.opBoolean","COPY",FACE,{"derivedFrom":makeQuery(id+"F19.opExtrude","CAP_FACE",FACE,{"disambiguationData":[OSD([sQuery(id+"F18.wireOp",EDGE,"E196.bottom"),sQuery(id+"F18.wireOp",EDGE,"E196.top"),sQuery(id+"F18.wireOp",EDGE,"E196.left"),sQuery(id+"F18.wireOp",EDGE,"E196.right")])],"isStart":false})});
            var sketch = newSketch(context, id + "F24", { "sketchPlane" : qUnion([Q0])});
            skLineSegment(sketch, "E199.0", {"start": v(272.92, 163.5) * mm, "end": v(272.92, 218.5) * mm});
            skLineSegment(sketch, "E199.1", {"start": v(235, 163.5) * mm, "end": v(272.92, 163.5) * mm});
            skLineSegment(sketch, "E199.2", {"start": v(235, 218.5) * mm, "end": v(235, 163.5) * mm});
            skLineSegment(sketch, "E199.3", {"start": v(272.92, 218.5) * mm, "end": v(235, 218.5) * mm});
            skSolve(sketch);
        }
        {
            var Q0;
            Q0=makeQuery(id+"F24.imprint","IMPRINT",FACE,{"disambiguationData":[TD([[makeQuery(id+"F24.imprint","IMPRINT",EDGE,{"derivedFrom":sQuery(id+"F24.wireOp",EDGE,"E199.0")}),1.0]])]});
            extrude(context, id + "F25", {"entities" : qUnion([Q0]), "operationType" : NewBodyOperationType.REMOVE, "oppositeDirection" : true, "depth" : 5 * mm});
        }
        {
            var Q0;
            Q0=makeQuery(id+"F8.opExtrude","CAP_FACE",FACE,{"disambiguationData":[OSD([sQuery(id+"F7.wireOp",EDGE,"E180.bottom"),sQuery(id+"F7.wireOp",EDGE,"E180.top"),sQuery(id+"F7.wireOp",EDGE,"E180.left"),sQuery(id+"F7.wireOp",EDGE,"E180.right")])],"isStart":true});
            var sketch = newSketch(context, id + "F26", { "sketchPlane" : qUnion([Q0])});
            skLineSegment(sketch, "E200.0", {"start": v(290, 406) * mm, "end": v(96, 406) * mm, "construction": true});
            skLineSegment(sketch, "E201.0", {"start": v(96, 124) * mm, "end": v(96, 406) * mm, "construction": true});
            skCircle(sketch, "E202.0", {"center": v(106, 366) * mm, "radius": 2.5 * mm, "construction": true});
            skLineSegment(sketch, "E203", {"start": v(96, 321) * mm, "end": v(239, 321) * mm});
            skLineSegment(sketch, "E204", {"start": v(239, 321) * mm, "end": v(239, 406) * mm});
            skLineSegment(sketch, "E205", {"start": v(224, 406) * mm, "end": v(224, 326) * mm});
            skLineSegment(sketch, "E206", {"start": v(224, 326) * mm, "end": v(96, 326) * mm});
            skLineSegment(sketch, "E207", {"start": v(96, 366) * mm, "end": v(290, 366) * mm, "construction": true});
            skLineSegment(sketch, "E208", {"start": v(96, 321) * mm, "end": v(96, 326) * mm});
            skLineSegment(sketch, "E209", {"start": v(224, 406) * mm, "end": v(239, 406) * mm});
            skSolve(sketch);
        }
        {
            var Q0;
            Q0 = qSketchRegion(id + "F26", true);
            extrude(context, id + "F27", {"entities" : qUnion([Q0]), "operationType" : NewBodyOperationType.ADD, "depth" : 5 * mm});
        }
        {
            var Q0;
            Q0=makeQuery(id+"F27.opExtrude","CAP_FACE",FACE,{"disambiguationData":[OSD([sQuery(id+"F26.wireOp",EDGE,"E203"),sQuery(id+"F26.wireOp",EDGE,"E204"),sQuery(id+"F26.wireOp",EDGE,"E205"),sQuery(id+"F26.wireOp",EDGE,"E206"),sQuery(id+"F26.wireOp",EDGE,"E208"),sQuery(id+"F26.wireOp",EDGE,"E209")])],"isStart":false});
            var sketch = newSketch(context, id + "F28", { "sketchPlane" : qUnion([Q0])});
            skLineSegment(sketch, "E210.0", {"start": v(224, 406) * mm, "end": v(224, 326) * mm});
            skLineSegment(sketch, "E211.0", {"start": v(239, 321) * mm, "end": v(239, 406) * mm});
            skLineSegment(sketch, "E212.0", {"start": v(239, 406) * mm, "end": v(224, 406) * mm});
            skLineSegment(sketch, "E213", {"start": v(224, 326) * mm, "end": v(224, 321) * mm});
            skLineSegment(sketch, "E214", {"start": v(224, 321) * mm, "end": v(239, 321) * mm});
            skSolve(sketch);
        }
        {
            var Q0;
            Q0 = qSketchRegion(id + "F28", true);
            var Q1;
            Q1=makeQuery(id+"F4.boolean.opBoolean","COPY",FACE,{"derivedFrom":makeQuery(id+"F4.opExtrude","CAP_FACE",FACE,{"disambiguationData":[OSD([sQuery(id+"F3.wireOp",EDGE,"E168"),sQuery(id+"F3.wireOp",EDGE,"E169"),sQuery(id+"F3.wireOp",EDGE,"E170.0"),sQuery(id+"F3.wireOp",EDGE,"E171")])],"isStart":false})});
            extrude(context, id + "F29", {"entities" : qUnion([Q0]), "operationType" : NewBodyOperationType.ADD, "endBound" : BoundingType.UP_TO_SURFACE, "endBoundEntityFace" : qUnion([Q1]), "depth" : 25 * mm});
        }
        {
            var Q0;
            Q0=makeQuery(id+"F27.boolean.opBoolean","SPLIT",FACE,{"disambiguationData":[TD([makeQuery(id+"F12.boolean.opBoolean","COPY",FACE,{"derivedFrom":makeQuery(id+"F12.opExtrude","SWEPT_FACE",FACE,{"disambiguationData":[OSD([sQuery(id+"F11.wireOp",EDGE,"E183")])]})})])],"derivedFrom":makeQuery(id+"F8.opExtrude","CAP_FACE",FACE,{"disambiguationData":[OSD([sQuery(id+"F7.wireOp",EDGE,"E180.bottom"),sQuery(id+"F7.wireOp",EDGE,"E180.top"),sQuery(id+"F7.wireOp",EDGE,"E180.left"),sQuery(id+"F7.wireOp",EDGE,"E180.right")])],"isStart":true})});
            var sketch = newSketch(context, id + "F30", { "sketchPlane" : qUnion([Q0])});
            skLineSegment(sketch, "E215.0", {"start": v(224, 406) * mm, "end": v(224, 326) * mm});
            skLineSegment(sketch, "E216", {"start": v(224, 406) * mm, "end": v(179, 406) * mm});
            skLineSegment(sketch, "E217", {"start": v(179, 406) * mm, "end": v(179, 326) * mm});
            skLineSegment(sketch, "E218", {"start": v(179, 326) * mm, "end": v(224, 326) * mm});
            skSolve(sketch);
        }
        {
            var Q0;
            Q0 = qSketchRegion(id + "F30", true);
            extrude(context, id + "F31", {"entities" : qUnion([Q0]), "operationType" : NewBodyOperationType.ADD, "depth" : 55 * mm});
        }
        {
            var Q0;
            Q0=makeQuery(id+"F31.opExtrude","SWEPT_FACE",FACE,{"disambiguationData":[OSD([sQuery(id+"F30.wireOp",EDGE,"E218")])]});
            var Q1;
            Q1=makeQuery(id+"F29.boolean.opBoolean","MERGE",FACE,{"derivedFrom":[makeQuery(id+"F27.opExtrude","SWEPT_FACE",FACE,{"disambiguationData":[OSD([sQuery(id+"F26.wireOp",EDGE,"E203")])]}),makeQuery(id+"F29.opExtrude","SWEPT_FACE",FACE,{"disambiguationData":[OSD([sQuery(id+"F28.wireOp",EDGE,"E214")])]})]});
            extrude(context, id + "F32", {"entities" : qUnion([Q0]), "operationType" : NewBodyOperationType.ADD, "endBound" : BoundingType.UP_TO_SURFACE, "endBoundEntityFace" : qUnion([Q1]), "depth" : 25 * mm});
        }
        {
            var Q0;
            Q0=makeQuery(id+"F32.boolean.opBoolean","MERGE",FACE,{"derivedFrom":[makeQuery(id+"F29.boolean.opBoolean","MERGE",FACE,{"derivedFrom":[makeQuery(id+"F27.opExtrude","SWEPT_FACE",FACE,{"disambiguationData":[OSD([sQuery(id+"F26.wireOp",EDGE,"E203")])]}),makeQuery(id+"F29.opExtrude","SWEPT_FACE",FACE,{"disambiguationData":[OSD([sQuery(id+"F28.wireOp",EDGE,"E214")])]})]}),makeQuery(id+"F32.opExtrude","CAP_FACE",FACE,{"disambiguationData":[OSD([sQuery(id+"F30.wireOp",EDGE,"E218")])],"isStart":false})]});
            var sketch = newSketch(context, id + "F33", { "sketchPlane" : qUnion([Q0])});
            skLineSegment(sketch, "E219.0", {"start": v(179, 55) * mm, "end": v(224, 55) * mm});
            skLineSegment(sketch, "E220.0", {"start": v(179, 5) * mm, "end": v(179, 55) * mm});
            skLineSegment(sketch, "E221.0", {"start": v(96, 5) * mm, "end": v(179, 5) * mm});
            skLineSegment(sketch, "E222", {"start": v(224, 55) * mm, "end": v(224, 190) * mm});
            skLineSegment(sketch, "E223", {"start": v(96, 190) * mm, "end": v(96, 5) * mm});
            skPoint(sketch, "E224.orphan", {"position": v(290, 220) * mm});
            skLineSegment(sketch, "E225", {"start": v(96, 190) * mm, "end": v(224, 190) * mm});
            skPoint(sketch, "E226.orphan", {"position": v(96, 220) * mm});
            skSolve(sketch);
        }
        {
            var Q0;
            Q0 = qSketchRegion(id + "F33", true);
            var Q1;
            Q1=makeQuery(id+"F27.opExtrude","SWEPT_FACE",FACE,{"disambiguationData":[OSD([sQuery(id+"F26.wireOp",EDGE,"E206")])]});
            extrude(context, id + "F34", {"entities" : qUnion([Q0]), "endBound" : BoundingType.UP_TO_SURFACE, "oppositeDirection" : true, "endBoundEntityFace" : qUnion([Q1]), "depth" : 5 * mm});
        }
        {
            var Q0;
            Q0=makeQuery(id+"F29.opExtrude","CAP_FACE",FACE,{"disambiguationData":[OSD([sQuery(id+"F28.wireOp",EDGE,"E210.0"),sQuery(id+"F28.wireOp",EDGE,"E211.0"),sQuery(id+"F28.wireOp",EDGE,"E212.0"),sQuery(id+"F28.wireOp",EDGE,"E213"),sQuery(id+"F28.wireOp",EDGE,"E214")])],"isStart":false});
            var Q1;
            Q1=makeQuery(id+"F34.opExtrude","SWEPT_FACE",FACE,{"disambiguationData":[OSD([sQuery(id+"F33.wireOp",EDGE,"E225")])]});
            extrude(context, id + "F35", {"entities" : qUnion([Q0]), "operationType" : NewBodyOperationType.ADD, "endBound" : BoundingType.UP_TO_SURFACE, "endBoundEntityFace" : qUnion([Q1]), "depth" : 40 * mm});
        }
        {
            var Q0;
            Q0=makeQuery(id+"F6.boolean.opBoolean","MERGE",FACE,{"derivedFrom":[makeQuery(id+"F2.opExtrude","SWEPT_FACE",FACE,{"disambiguationData":[OSD([sQuery(id+"F1.wireOp",EDGE,"E144.0"),sQuery(id+"F1.wireOp",EDGE,"E146.0"),sQuery(id+"F1.wireOp",EDGE,"E153")])]}),makeQuery(id+"F6.opExtrude","SWEPT_FACE",FACE,{"disambiguationData":[OSD([sQuery(id+"F5.wireOp",EDGE,"E175.0")])]})]});
            var sketch = newSketch(context, id + "F36", { "sketchPlane" : qUnion([Q0])});
            skLineSegment(sketch, "E227.0.0", {"start": v(224, 190) * mm, "end": v(224, 55) * mm, "construction": true});
            skLineSegment(sketch, "E227.0.1", {"start": v(224, 55) * mm, "end": v(179, 55) * mm, "construction": true});
            skLineSegment(sketch, "E227.0.2", {"start": v(179, 55) * mm, "end": v(179, 5) * mm, "construction": true});
            skLineSegment(sketch, "E227.0.3", {"start": v(179, 5) * mm, "end": v(96, 5) * mm, "construction": true});
            skLineSegment(sketch, "E227.0.4", {"start": v(96, 5) * mm, "end": v(96, 0) * mm, "construction": true});
            skLineSegment(sketch, "E228", {"start": v(239, 190) * mm, "end": v(290, 190) * mm});
            skLineSegment(sketch, "E229", {"start": v(290, 190) * mm, "end": v(290, 182.5) * mm});
            skLineSegment(sketch, "E230", {"start": v(290, 182.5) * mm, "end": v(239, 182.5) * mm});
            skLineSegment(sketch, "E231", {"start": v(239, 182.5) * mm, "end": v(239, 190) * mm});
            skLineSegment(sketch, "E232", {"start": v(239, 142.5) * mm, "end": v(290, 142.5) * mm});
            skLineSegment(sketch, "E233", {"start": v(290, 142.5) * mm, "end": v(290, 135) * mm});
            skLineSegment(sketch, "E234", {"start": v(290, 135) * mm, "end": v(239, 135) * mm});
            skLineSegment(sketch, "E235", {"start": v(239, 135) * mm, "end": v(239, 142.5) * mm});
            skLineSegment(sketch, "E236", {"start": v(239, 95) * mm, "end": v(290, 95) * mm});
            skLineSegment(sketch, "E237", {"start": v(290, 95) * mm, "end": v(290, 87.5) * mm});
            skLineSegment(sketch, "E238", {"start": v(290, 87.5) * mm, "end": v(239, 87.5) * mm});
            skLineSegment(sketch, "E239", {"start": v(239, 87.5) * mm, "end": v(239, 95) * mm});
            skLineSegment(sketch, "E240", {"start": v(239, 47.5) * mm, "end": v(290, 47.5) * mm});
            skLineSegment(sketch, "E241", {"start": v(290, 47.5) * mm, "end": v(290, 40) * mm});
            skLineSegment(sketch, "E242", {"start": v(290, 40) * mm, "end": v(239, 40) * mm});
            skLineSegment(sketch, "E243", {"start": v(239, 40) * mm, "end": v(239, 47.5) * mm});
            skLineSegment(sketch, "E244", {"start": v(239, 190) * mm, "end": v(239, 0) * mm, "construction": true});
            skLineSegment(sketch, "E245", {"start": v(224, 190) * mm, "end": v(239, 190) * mm});
            skLineSegment(sketch, "E246", {"start": v(290, 190) * mm, "end": v(290, 0) * mm, "construction": true});
            skSolve(sketch);
        }
        {
            var Q0;
            {var subQ0=sQuery(id+"F36.wireOp",EDGE,"E242");Q0=makeQuery(id+"F36.imprint","IMPRINT",FACE,{"disambiguationData":[TD([[makeQuery(id+"F36.imprint","IMPRINT",EDGE,{"derivedFrom":subQ0}),1.0]])]});}
            var sketch = newSketch(context, id + "F37", { "sketchPlane" : qUnion([Q0])});
            skLineSegment(sketch, "E247.0.0", {"start": v(239, 40) * mm, "end": v(290, 40) * mm});
            skLineSegment(sketch, "E247.0.1", {"start": v(290, 40) * mm, "end": v(290, 47.5) * mm});
            skLineSegment(sketch, "E247.0.2", {"start": v(290, 47.5) * mm, "end": v(239, 47.5) * mm});
            skLineSegment(sketch, "E247.0.3", {"start": v(239, 47.5) * mm, "end": v(239, 40) * mm});
            skSolve(sketch);
        }
        {
            var Q0;
            Q0 = qSketchRegion(id + "F37", true);
            extrude(context, id + "F38", {"entities" : qUnion([Q0]), "depth" : 85 * mm});
        }
        {
            var Q0;
            {var subQ0=sQuery(id+"F36.wireOp",EDGE,"E238");Q0=makeQuery(id+"F36.imprint","IMPRINT",FACE,{"disambiguationData":[TD([[makeQuery(id+"F36.imprint","IMPRINT",EDGE,{"derivedFrom":subQ0}),1.0]])]});}
            var sketch = newSketch(context, id + "F39", { "sketchPlane" : qUnion([Q0])});
            skLineSegment(sketch, "E248.0.0", {"start": v(239, 87.5) * mm, "end": v(290, 87.5) * mm});
            skLineSegment(sketch, "E248.0.1", {"start": v(290, 87.5) * mm, "end": v(290, 95) * mm});
            skLineSegment(sketch, "E248.0.2", {"start": v(290, 95) * mm, "end": v(239, 95) * mm});
            skLineSegment(sketch, "E248.0.3", {"start": v(239, 95) * mm, "end": v(239, 87.5) * mm});
            skSolve(sketch);
        }
        {
            var Q0;
            Q0 = qSketchRegion(id + "F39", true);
            extrude(context, id + "F40", {"entities" : qUnion([Q0]), "depth" : (85 - 14.2) * mm});
        }
        {
            var Q0;
            {var subQ0=sQuery(id+"F36.wireOp",EDGE,"E234");Q0=makeQuery(id+"F36.imprint","IMPRINT",FACE,{"disambiguationData":[TD([[makeQuery(id+"F36.imprint","IMPRINT",EDGE,{"derivedFrom":subQ0}),1.0]])]});}
            var sketch = newSketch(context, id + "F41", { "sketchPlane" : qUnion([Q0])});
            skLineSegment(sketch, "E249.0.0", {"start": v(239, 135) * mm, "end": v(290, 135) * mm});
            skLineSegment(sketch, "E249.0.1", {"start": v(290, 135) * mm, "end": v(290, 142.5) * mm});
            skLineSegment(sketch, "E249.0.2", {"start": v(290, 142.5) * mm, "end": v(239, 142.5) * mm});
            skLineSegment(sketch, "E249.0.3", {"start": v(239, 142.5) * mm, "end": v(239, 135) * mm});
            skSolve(sketch);
        }
        {
            var Q0;
            Q0 = qSketchRegion(id + "F41", true);
            extrude(context, id + "F42", {"entities" : qUnion([Q0]), "depth" : (42.5 + 14.2) * mm});
        }
        {
            var Q0;
            {var subQ0=sQuery(id+"F36.wireOp",EDGE,"E230");Q0=makeQuery(id+"F36.imprint","IMPRINT",FACE,{"disambiguationData":[TD([[makeQuery(id+"F36.imprint","IMPRINT",EDGE,{"derivedFrom":subQ0}),1.0]])]});}
            var sketch = newSketch(context, id + "F43", { "sketchPlane" : qUnion([Q0])});
            skLineSegment(sketch, "E250.0.0", {"start": v(239, 182.5) * mm, "end": v(290, 182.5) * mm});
            skLineSegment(sketch, "E250.0.1", {"start": v(290, 182.5) * mm, "end": v(290, 190) * mm});
            skLineSegment(sketch, "E250.0.2", {"start": v(290, 190) * mm, "end": v(239, 190) * mm});
            skLineSegment(sketch, "E250.0.3", {"start": v(239, 190) * mm, "end": v(239, 182.5) * mm});
            skSolve(sketch);
        }
        {
            var Q0;
            Q0 = qSketchRegion(id + "F43", true);
            extrude(context, id + "F44", {"entities" : qUnion([Q0]), "depth" : (85 - 24 - 18.5) * mm});
        }
    });
